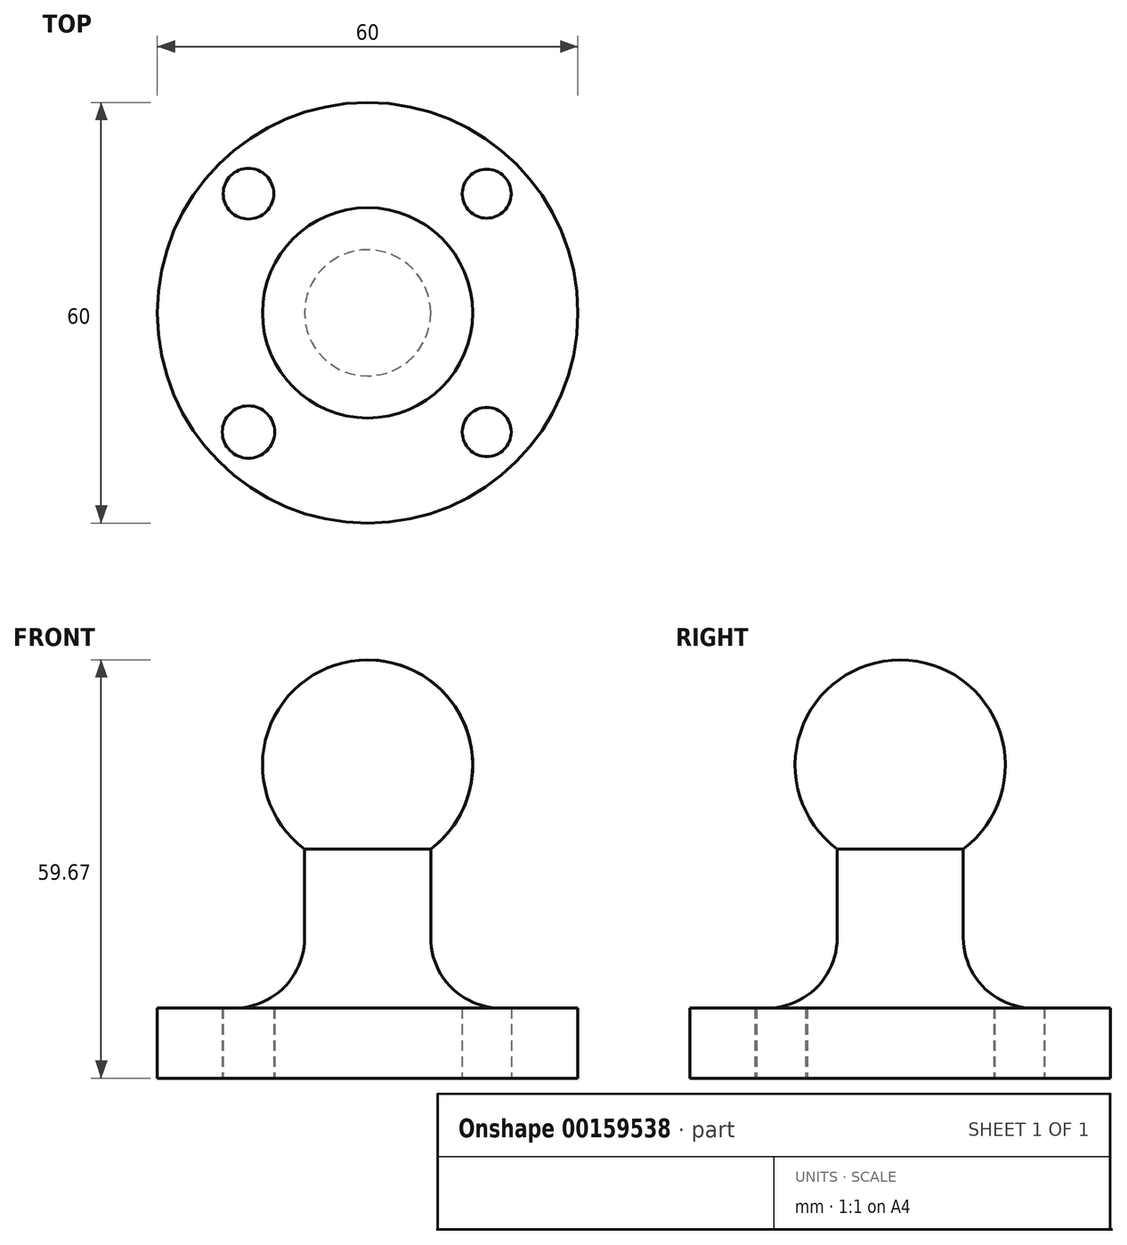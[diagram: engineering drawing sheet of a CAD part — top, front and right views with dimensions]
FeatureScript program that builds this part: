
annotation { "Feature Type Name" : "Feature", "Feature Type Description" : "" }
export const myFeature = defineFeature(function(context is Context, id is Id, definition is map)
    precondition{}
    {
        {
            var Q0;
            Q0=qCreatedBy(makeId("Front.planeOp"),FACE);
            var sketch = newSketch(context, id + "F0", { "sketchPlane" : qUnion([Q0])});
            skLineSegment(sketch, "E0.bottom", {"start": v(0, 19.23) * mm, "end": v(-9, 19.23) * mm});
            skLineSegment(sketch, "E0.top", {"start": v(0, -5.77) * mm, "end": v(-9, -5.77) * mm});
            skLineSegment(sketch, "E0.left", {"start": v(0, 19.23) * mm, "end": v(0, -5.77) * mm});
            skLineSegment(sketch, "E0.right", {"start": v(-9, 19.23) * mm, "end": v(-9, -5.77) * mm});
            skArc(sketch, "E1", {"start": v(0, 43.9) * mm, "mid": v(-15, 28.9) * mm, "end": v(0, 13.9) * mm});
            skLineSegment(sketch, "E2", {"start": v(0, 49.66) * mm, "end": v(0, -13.68) * mm});
            skLineSegment(sketch, "E3.bottom", {"start": v(0, -5.77) * mm, "end": v(-30, -5.77) * mm});
            skLineSegment(sketch, "E3.top", {"start": v(0, -15.77) * mm, "end": v(-30, -15.77) * mm});
            skLineSegment(sketch, "E3.left", {"start": v(0, -5.77) * mm, "end": v(0, -15.77) * mm});
            skLineSegment(sketch, "E3.right", {"start": v(-30, -5.77) * mm, "end": v(-30, -15.77) * mm});
            skSolve(sketch);
        }
        {
            var Q0;
            Q0 = qSketchRegion(id + "F0", true);
            var Q1;
            Q1=sQuery(id+"F0.wireOp",EDGE,"E2");
            revolve(context, id + "F1", {"entities" : qUnion([Q0]), "axis" : qUnion([Q1]), "revolveType" : RevolveType.FULL});
        }
        {
            var Q0;
            Q0=makeQuery(id+"F1.opRevolve","SWEPT_FACE",FACE,{"disambiguationData":[OSD([sQuery(id+"F0.wireOp",EDGE,"E3.top")])]});
            var sketch = newSketch(context, id + "F2", { "sketchPlane" : qUnion([Q0])});
            skCircle(sketch, "E4", {"center": v(-17, 17) * mm, "radius": 3.73 * mm});
            skCircle(sketch, "E5", {"center": v(17, 17) * mm, "radius": 3.5 * mm});
            skCircle(sketch, "E6", {"center": v(-17, -17) * mm, "radius": 3.61 * mm});
            skCircle(sketch, "E7", {"center": v(17, -17) * mm, "radius": 3.5 * mm});
            skSolve(sketch);
        }
        {
            var Q0;
            Q0 = qSketchRegion(id + "F2", true);
            extrude(context, id + "F3", {"entities" : qUnion([Q0]), "operationType" : NewBodyOperationType.REMOVE, "oppositeDirection" : true, "depth" : 25 * mm});
        }
        {
            var Q0;
            Q0=makeQuery(id+"F1.opRevolve","SWEPT_EDGE",EDGE,{"disambiguationData":[OSD([sQuery(id+"F0.wireOp",EDGE,"E0.right"),sQuery(id+"F0.wireOp",EDGE,"E3.bottom")])]});
            fillet(context, id + "F4", {"entities" : qUnion([Q0]), "radius" : 10 * mm, "tangentPropagation" : true, "allowEdgeOverflow" : false});
        }
    });
